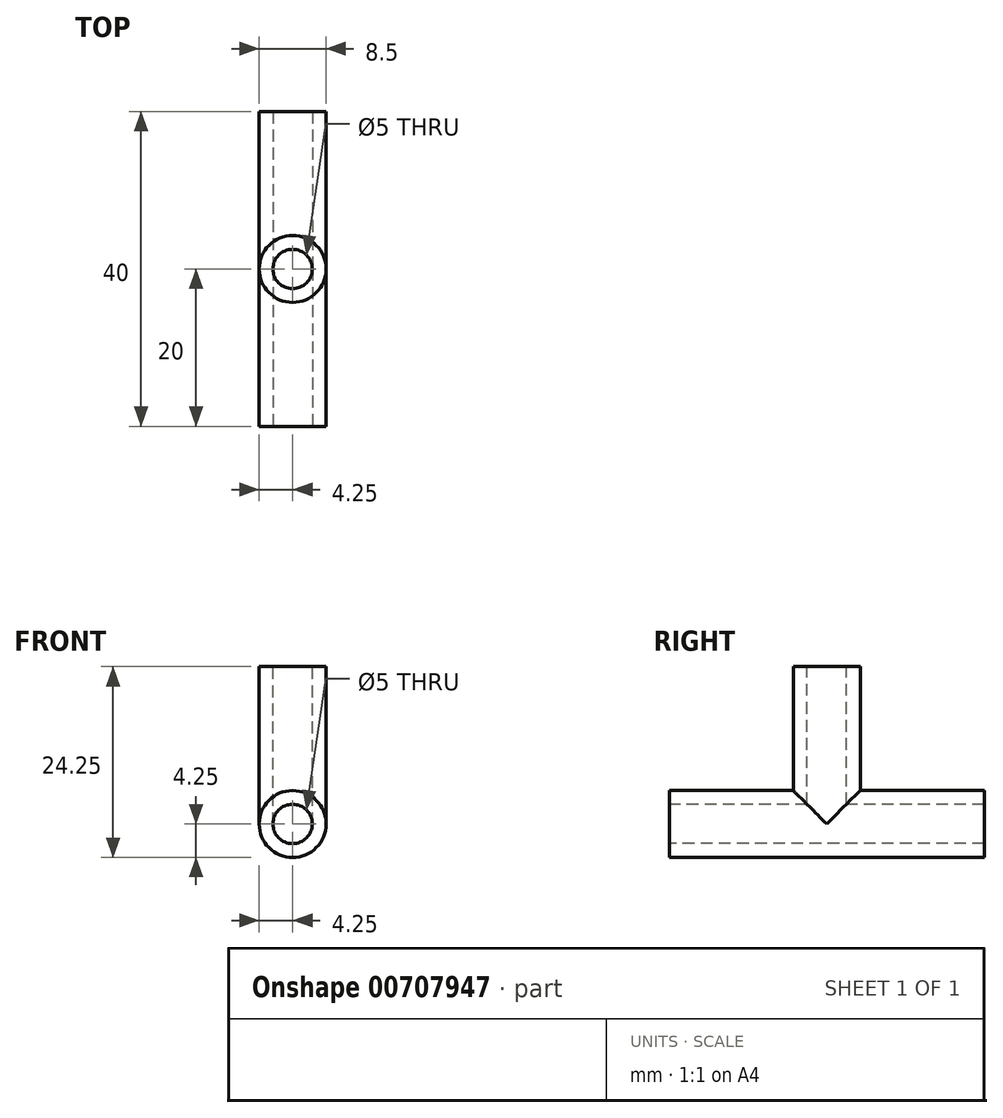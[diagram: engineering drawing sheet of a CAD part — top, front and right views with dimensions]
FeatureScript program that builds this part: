
annotation { "Feature Type Name" : "Feature", "Feature Type Description" : "" }
export const myFeature = defineFeature(function(context is Context, id is Id, definition is map)
    precondition{}
    {
        {
            var Q0;
            Q0=qCreatedBy(makeId("Top.planeOp"),FACE);
            var sketch = newSketch(context, id + "F0", { "sketchPlane" : qUnion([Q0])});
            skCircle(sketch, "E0", {"center": v(0, 0) * mm, "radius": 4.25 * mm});
            skSolve(sketch);
        }
        {
            var Q0;
            Q0=qCreatedBy(makeId("Front.planeOp"),FACE);
            var sketch = newSketch(context, id + "F1", { "sketchPlane" : qUnion([Q0])});
            skCircle(sketch, "E1", {"center": v(0, 0) * mm, "radius": 4.25 * mm});
            skSolve(sketch);
        }
        {
            var Q0;
            Q0=makeQuery(id+"F1.imprint","IMPRINT",FACE,{"disambiguationData":[TD([[makeQuery(id+"F1.imprint","IMPRINT",EDGE,{"derivedFrom":sQuery(id+"F1.wireOp",EDGE,"E1")}),1.0]])]});
            extrude(context, id + "F2", {"entities" : qUnion([Q0]), "endBound" : BoundingType.SYMMETRIC, "depth" : 40 * mm, "offsetDistance" : 25 * mm});
        }
        {
            var Q0;
            Q0=makeQuery(id+"F2.opExtrude","CAP_FACE",FACE,{"disambiguationData":[OSD([sQuery(id+"F1.wireOp",EDGE,"E1")])],"isStart":false});
            var sketch = newSketch(context, id + "F3", { "sketchPlane" : qUnion([Q0])});
            skCircle(sketch, "E2", {"center": v(0, 0) * mm, "radius": 2.5 * mm});
            skSolve(sketch);
        }
        {
            var Q0;
            Q0 = qSketchRegion(id + "F0", true);
            extrude(context, id + "F4", {"entities" : qUnion([Q0]), "operationType" : NewBodyOperationType.ADD, "depth" : 20 * mm, "offsetDistance" : 25 * mm});
        }
        {
            var Q0;
            Q0 = qSketchRegion(id + "F3", true);
            extrude(context, id + "F5", {"entities" : qUnion([Q0]), "operationType" : NewBodyOperationType.REMOVE, "oppositeDirection" : true, "depth" : 40 * mm, "offsetDistance" : 25 * mm});
        }
        {
            var Q0;
            Q0=makeQuery(id+"F4.opExtrude","CAP_FACE",FACE,{"disambiguationData":[OSD([sQuery(id+"F0.wireOp",EDGE,"E0")])],"isStart":false});
            var sketch = newSketch(context, id + "F6", { "sketchPlane" : qUnion([Q0])});
            skCircle(sketch, "E3", {"center": v(0, 0) * mm, "radius": 2.5 * mm});
            skSolve(sketch);
        }
        {
            var Q0;
            Q0 = qSketchRegion(id + "F6", true);
            extrude(context, id + "F7", {"entities" : qUnion([Q0]), "operationType" : NewBodyOperationType.REMOVE, "oppositeDirection" : true, "depth" : 20 * mm, "offsetDistance" : 25 * mm});
        }
    });
